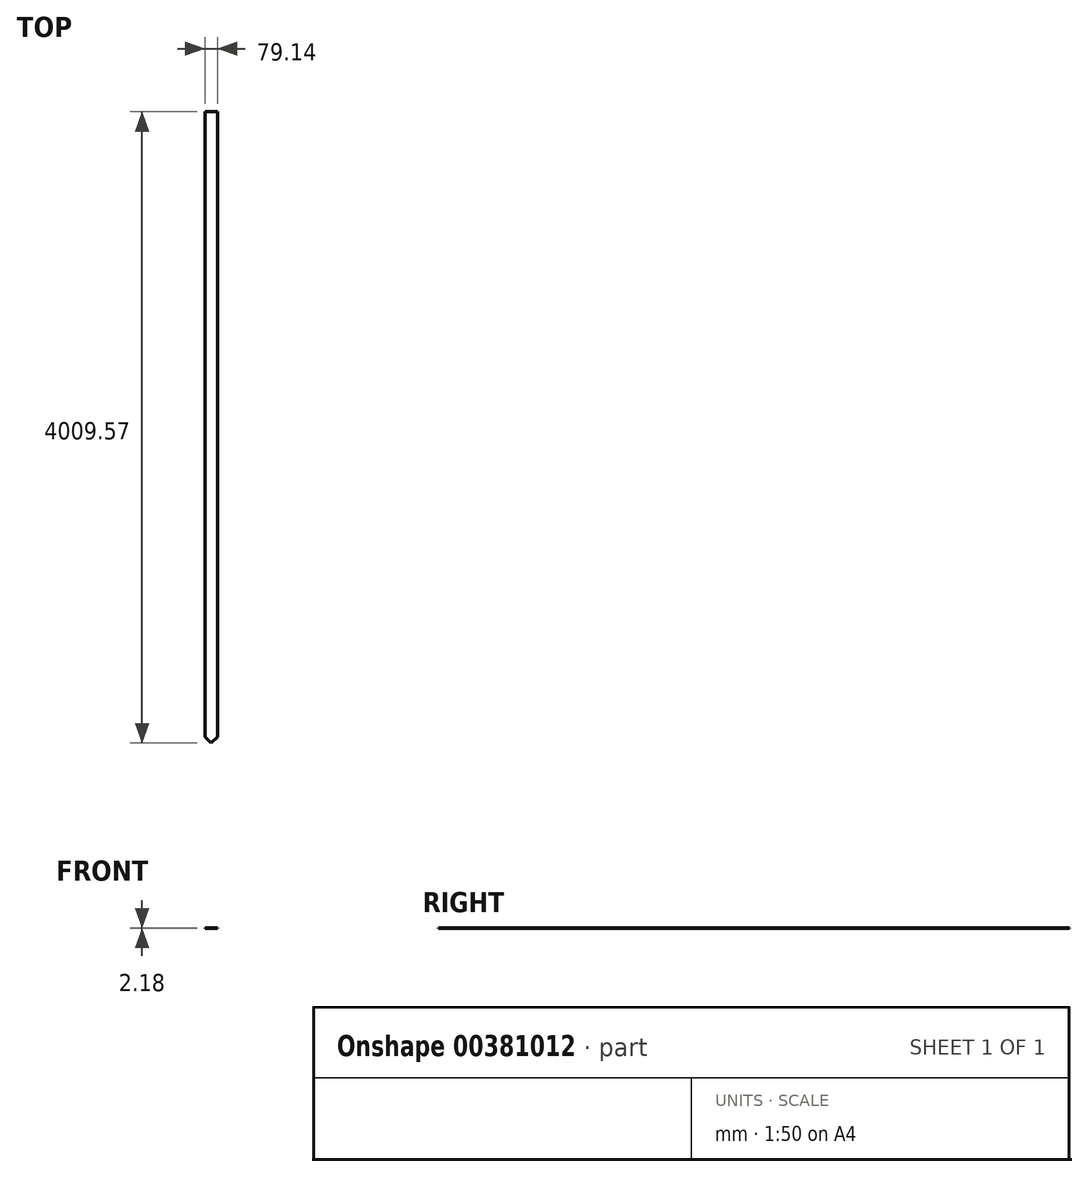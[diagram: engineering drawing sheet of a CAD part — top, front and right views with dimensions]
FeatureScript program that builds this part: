
annotation { "Feature Type Name" : "Feature", "Feature Type Description" : "" }
export const myFeature = defineFeature(function(context is Context, id is Id, definition is map)
    precondition{}
    {
        {
            var Q0;
            Q0=qCreatedBy(makeId("Front.planeOp"),FACE);
            var sketch = newSketch(context, id + "F0", { "sketchPlane" : qUnion([Q0])});
            skLineSegment(sketch, "E0.bottom", {"start": v(-39.57, -1.09) * mm, "end": v(39.57, -1.09) * mm});
            skLineSegment(sketch, "E0.top", {"start": v(-39.57, 1.09) * mm, "end": v(39.57, 1.09) * mm});
            skLineSegment(sketch, "E0.left", {"start": v(-39.57, -1.09) * mm, "end": v(-39.57, 1.09) * mm});
            skLineSegment(sketch, "E0.right", {"start": v(39.57, -1.09) * mm, "end": v(39.57, 1.09) * mm});
            skPoint(sketch, "E0.middle", {"position": v(0, 0) * mm});
            skSolve(sketch);
        }
        {
            var Q0;
            Q0=makeQuery(id+"F0.imprint","IMPRINT",FACE,{"disambiguationData":[TD([[makeQuery(id+"F0.imprint","IMPRINT",EDGE,{"derivedFrom":sQuery(id+"F0.wireOp",EDGE,"E0.bottom")}),1.0]])]});
            extrude(context, id + "F1", {"entities" : qUnion([Q0]), "depth" : 4010 * mm});
        }
        {
            var Q0;
            Q0=makeQuery(id+"F1.opExtrude","CAP_EDGE",EDGE,{"disambiguationData":[OSD([sQuery(id+"F0.wireOp",EDGE,"E0.right")])],"isStart":false});
            var Q1;
            Q1=makeQuery(id+"F1.opExtrude","CAP_EDGE",EDGE,{"disambiguationData":[OSD([sQuery(id+"F0.wireOp",EDGE,"E0.left")])],"isStart":false});
            chamfer(context, id + "F2", {"entities" : qUnion([Q0, Q1]), "width" : 40 * mm, "tangentPropagation" : true});
        }
    });
